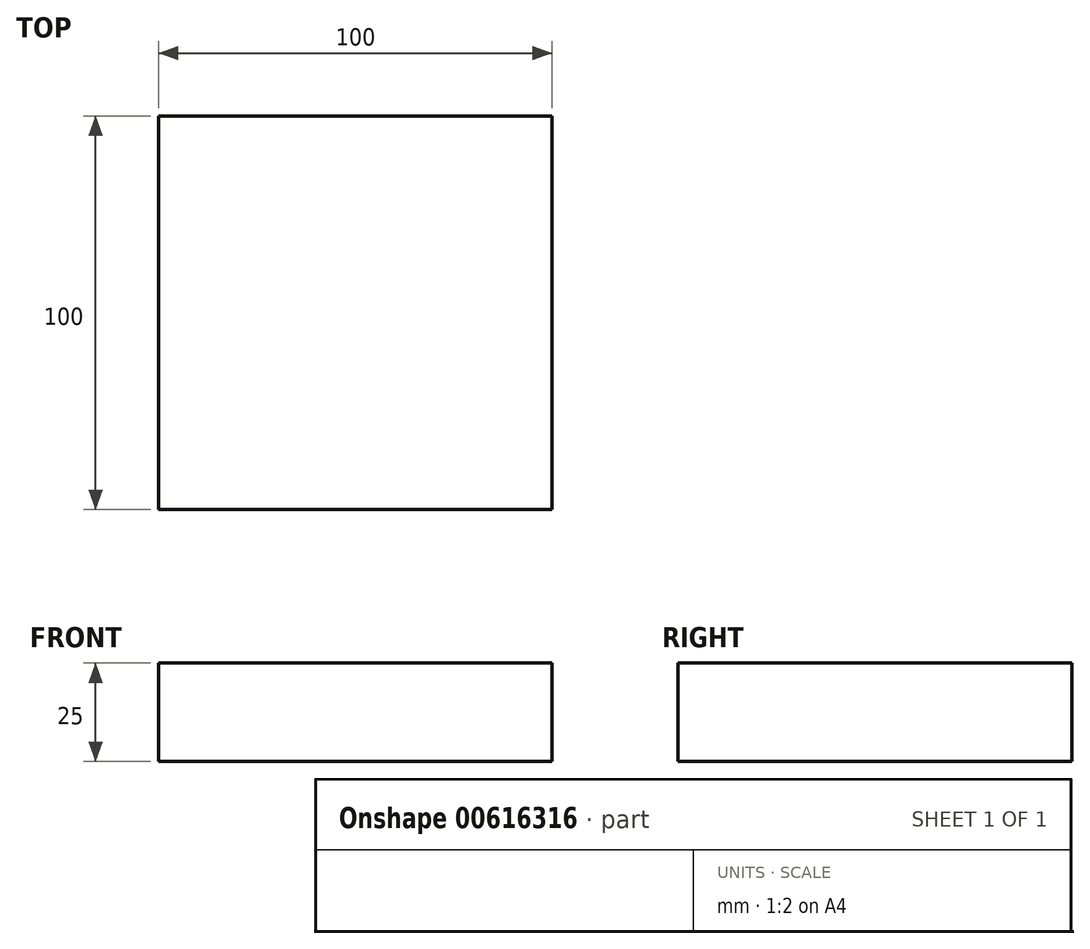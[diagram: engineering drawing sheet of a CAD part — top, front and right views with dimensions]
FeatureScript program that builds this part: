
annotation { "Feature Type Name" : "Feature", "Feature Type Description" : "" }
export const myFeature = defineFeature(function(context is Context, id is Id, definition is map)
    precondition{}
    {
        {
            var Q0;
            Q0=qCreatedBy(makeId("Top.planeOp"),FACE);
            var sketch = newSketch(context, id + "F0", { "sketchPlane" : qUnion([Q0])});
            skLineSegment(sketch, "E0.bottom", {"start": v(-50, 50) * mm, "end": v(50, 50) * mm});
            skLineSegment(sketch, "E0.top", {"start": v(-50, -50) * mm, "end": v(50, -50) * mm});
            skLineSegment(sketch, "E0.left", {"start": v(-50, 50) * mm, "end": v(-50, -50) * mm});
            skLineSegment(sketch, "E0.right", {"start": v(50, 50) * mm, "end": v(50, -50) * mm});
            skPoint(sketch, "E0.middle", {"position": v(0, 0) * mm});
            skSolve(sketch);
        }
        {
            var Q0;
            Q0 = qSketchRegion(id + "F0", true);
            extrude(context, id + "F1", {"entities" : qUnion([Q0]), "depth" : 25 * mm, "offsetDistance" : 25 * mm});
        }
    });
